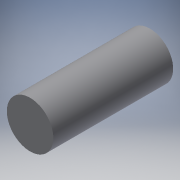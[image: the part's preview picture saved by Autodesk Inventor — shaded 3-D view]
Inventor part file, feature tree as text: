
AUTODESK INVENTOR PART (.ipt)
format: ipt  version: 2018.1 (Build 221171000, 171)  size: 91,648 bytes
history: native  units: mm
features: extrude x1, sketch x1
ambient origin geometry x8: Origin, YZ Plane, XZ Plane, XY Plane, X Axis, Y Axis, Z Axis, Center Point
bodies: Solid1 (feature_tree)
feature tree (2):
  extrude  "Extrusion1"  Depth=50.0mm TaperAngle=0.0deg
  sketch  "Sketch1"  dims[d0=19.4mm d1=50.0mm d2=0.0mm]
